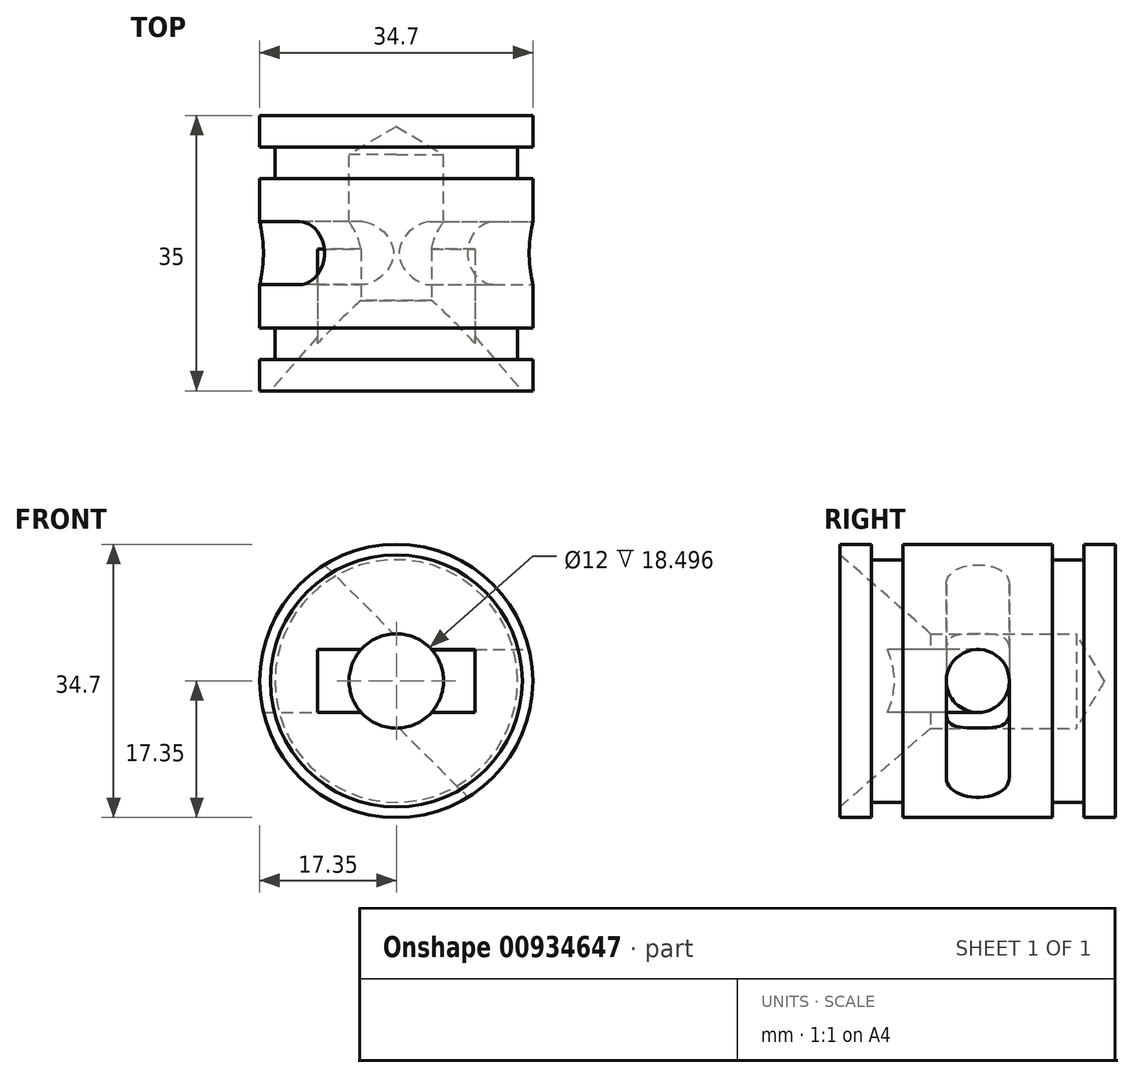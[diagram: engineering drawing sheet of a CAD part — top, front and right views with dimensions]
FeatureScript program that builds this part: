
annotation { "Feature Type Name" : "Feature", "Feature Type Description" : "" }
export const myFeature = defineFeature(function(context is Context, id is Id, definition is map)
    precondition{}
    {
        {
            var Q0;
            Q0=qCreatedBy(makeId("Front.planeOp"),FACE);
            var sketch = newSketch(context, id + "F0", { "sketchPlane" : qUnion([Q0])});
            skCircle(sketch, "E0", {"center": v(0, 0) * mm, "radius": 17.35 * mm});
            skCircle(sketch, "E1", {"center": v(0, 0) * mm, "radius": 16.35 * mm});
            skSolve(sketch);
        }
        {
            var Q0;
            Q0=makeQuery(id+"F0.imprint","IMPRINT",FACE,{"disambiguationData":[TD([[makeQuery(id+"F0.imprint","IMPRINT",EDGE,{"derivedFrom":sQuery(id+"F0.wireOp",EDGE,"E1")}),1.0]])]});
            var Q1;
            Q1=makeQuery(id+"F0.imprint","IMPRINT",FACE,{"disambiguationData":[TD([[makeQuery(id+"F0.imprint","IMPRINT",EDGE,{"derivedFrom":sQuery(id+"F0.wireOp",EDGE,"E0")}),1.0]])]});
            extrude(context, id + "F1", {"entities" : qUnion([Q0, Q1]), "oppositeDirection" : true, "depth" : 35 * mm, "offsetDistance" : 25 * mm, "symmetric" : true});
        }
        {
            var Q0;
            Q0=qCreatedBy(makeId("Right.planeOp"),FACE);
            var sketch = newSketch(context, id + "F2", { "sketchPlane" : qUnion([Q0])});
            skLineSegment(sketch, "E2.bottom", {"start": v(-13.5, 20.4) * mm, "end": v(-9.5, 20.4) * mm});
            skLineSegment(sketch, "E2.top", {"start": v(-13.5, 15.4) * mm, "end": v(-9.5, 15.4) * mm});
            skLineSegment(sketch, "E2.left", {"start": v(-13.5, 20.4) * mm, "end": v(-13.5, 15.4) * mm});
            skLineSegment(sketch, "E2.right", {"start": v(-9.5, 20.4) * mm, "end": v(-9.5, 15.4) * mm});
            skLineSegment(sketch, "E3.MirrorCS", {"start": v(13.5, 20.4) * mm, "end": v(9.5, 20.4) * mm});
            skLineSegment(sketch, "E4.MirrorCS", {"start": v(9.5, 20.4) * mm, "end": v(9.5, 15.4) * mm});
            skLineSegment(sketch, "E5.MirrorCS", {"start": v(13.5, 15.4) * mm, "end": v(9.5, 15.4) * mm});
            skLineSegment(sketch, "E6.MirrorCS", {"start": v(13.5, 20.4) * mm, "end": v(13.5, 15.4) * mm});
            skSolve(sketch);
        }
        {
            var Q0;
            Q0=makeQuery(id+"F2.imprint","IMPRINT",FACE,{"disambiguationData":[TD([[makeQuery(id+"F2.imprint","IMPRINT",EDGE,{"derivedFrom":sQuery(id+"F2.wireOp",EDGE,"E2.bottom")}),-1.0]])]});
            var Q1;
            Q1=makeQuery(id+"F2.imprint","IMPRINT",FACE,{"disambiguationData":[TD([[makeQuery(id+"F2.imprint","IMPRINT",EDGE,{"derivedFrom":sQuery(id+"F2.wireOp",EDGE,"E3.MirrorCS")}),1.0]])]});
            var Q2;
            Q2=makeQuery(id+"F1.opExtrude","SWEPT_FACE",FACE,{"disambiguationData":[OSD([sQuery(id+"F0.wireOp",EDGE,"E0")])]});
            revolve(context, id + "F3", {"operationType" : NewBodyOperationType.REMOVE, "surfaceOperationType" : NewSurfaceOperationType.NEW, "entities" : qUnion([Q0, Q1]), "axis" : qUnion([Q2]), "revolveType" : RevolveType.FULL, "oppositeDirection" : true});
        }
        {
            var Q0;
            Q0=makeQuery(id+"F1.opExtrude","CAP_FACE",FACE,{"disambiguationData":[OSD([sQuery(id+"F0.wireOp",EDGE,"E0")])],"isStart":true});
            var sketch = newSketch(context, id + "F4", { "sketchPlane" : qUnion([Q0])});
            skCircle(sketch, "E7", {"center": v(0, 0) * mm, "radius": 6 * mm});
            skLineSegment(sketch, "E8.bottom", {"start": v(10, -4) * mm, "end": v(-10, -4) * mm});
            skLineSegment(sketch, "E8.top", {"start": v(10, 4) * mm, "end": v(-10, 4) * mm});
            skLineSegment(sketch, "E8.left", {"start": v(10, -4) * mm, "end": v(10, 4) * mm});
            skLineSegment(sketch, "E8.right", {"start": v(-10, -4) * mm, "end": v(-10, 4) * mm});
            skSolve(sketch);
        }
        {
            var Q0;
            Q0=sQuery(id+"F4.wireOp",VERTEX,"E7.center");
            var Q1;
            Q1=makeQuery(id+"F1.opExtrude","SWEPT_BODY",BODY,{"disambiguationData":[OSD([sQuery(id+"F0.wireOp",EDGE,"E0")])]});
            hole(context, id + "F5", {"style" : HoleStyle.C_SINK, "endStyle" : HoleEndStyle.BLIND, "holeDiameter" : 12 * mm, "cSinkDiameter" : 32 * mm, "cSinkAngle" : 82 * degree, "majorDiameter" : 5 * mm, "holeDepth" : 30 * mm, "isTappedThrough" : true, "tappedDepth" : 40 * mm, "tapClearance" : 3, "startFromSketch" : true, "locations" : qUnion([Q0]), "scope" : qUnion([Q1])});
        }
        {
            var Q0;
            {var subQ5=sQuery(id+"F4.wireOp",EDGE,"E8.right");Q0=makeQuery(id+"F4.imprint","IMPRINT",FACE,{"disambiguationData":[TD([[makeQuery(id+"F4.imprint","IMPRINT",EDGE,{"derivedFrom":subQ5}),-1.0]])]});}
            var Q1;
            {var subQ5=sQuery(id+"F4.wireOp",EDGE,"E8.left");Q1=makeQuery(id+"F4.imprint","IMPRINT",FACE,{"disambiguationData":[TD([[makeQuery(id+"F4.imprint","IMPRINT",EDGE,{"derivedFrom":subQ5}),1.0]])]});}
            extrude(context, id + "F6", {"entities" : qUnion([Q0, Q1]), "operationType" : NewBodyOperationType.REMOVE, "oppositeDirection" : true, "depth" : 18 * mm, "offsetDistance" : 25 * mm});
        }
        {
            var Q0;
            Q0=qCreatedBy(makeId("Right.planeOp"),FACE);
            var sketch = newSketch(context, id + "F7", { "sketchPlane" : qUnion([Q0])});
            skCircle(sketch, "E9", {"center": v(0, 0) * mm, "radius": 4 * mm});
            skSolve(sketch);
        }
        {
            var Q0;
            Q0 = qSketchRegion(id + "F7", true);
            extrude(context, id + "F8", {"entities" : qUnion([Q0]), "operationType" : NewBodyOperationType.REMOVE, "oppositeDirection" : true, "depth" : 35 * mm, "offsetDistance" : 25 * mm, "symmetric" : true});
        }
        {
            var Q0;
            Q0=qCreatedBy(makeId("Right.planeOp"),FACE);
            var Q1;
            Q1=qCreatedBy(makeId("Top.planeOp"),FACE);
            cPlane(context, id + "F9", {"entities" : qUnion([Q0, Q1]), "cplaneType" : CPlaneType.MID_PLANE, "offset" : 25 * mm, "width" : 150 * mm, "height" : 150 * mm});
        }
        {
            var Q0;
            Q0=qCreatedBy(id+"F9.planeOp",FACE);
            var sketch = newSketch(context, id + "F10", { "sketchPlane" : qUnion([Q0])});
            skCircle(sketch, "E10", {"center": v(0, 0) * mm, "radius": 4 * mm});
            skSolve(sketch);
        }
        {
            var Q0;
            Q0=makeQuery(id+"F10.imprint","IMPRINT",FACE,{"disambiguationData":[TD([[makeQuery(id+"F10.imprint","IMPRINT",EDGE,{"derivedFrom":sQuery(id+"F10.wireOp",EDGE,"E10")}),1.0]])]});
            extrude(context, id + "F11", {"entities" : qUnion([Q0]), "operationType" : NewBodyOperationType.REMOVE, "oppositeDirection" : true, "depth" : 35 * mm, "offsetDistance" : 25 * mm, "symmetric" : true});
        }
        {
            var Q0;
            Q0=qCreatedBy(makeId("Front.planeOp"),FACE);
            var sketch = newSketch(context, id + "F12", { "sketchPlane" : qUnion([Q0])});
            skCircle(sketch, "E11.0", {"center": v(0, 0) * mm, "radius": 17.35 * mm});
            skLineSegment(sketch, "E12", {"start": v(-0.33, 6) * mm, "end": v(-9.1, 14.77) * mm});
            skLineSegment(sketch, "E13", {"start": v(-14.77, 9.1) * mm, "end": v(-9.66, 4) * mm});
            skLineSegment(sketch, "E14", {"start": v(14.77, -9.1) * mm, "end": v(9.66, -4) * mm});
            skLineSegment(sketch, "E15", {"start": v(0.33, -6) * mm, "end": v(9.1, -14.77) * mm});
            skLineSegment(sketch, "E16", {"start": v(0, 0) * mm, "end": v(-12.27, 12.27) * mm});
            skLineSegment(sketch, "E17", {"start": v(0, 0) * mm, "end": v(-17.35, 0) * mm});
            skLineSegment(sketch, "E18", {"start": v(0, 0) * mm, "end": v(12.27, -12.27) * mm});
            skLineSegment(sketch, "E19", {"start": v(0, 0) * mm, "end": v(17.35, 0) * mm});
            skSolve(sketch);
        }
        {
            var Q0;
            {var subQ2=sQuery(id+"F12.wireOp",EDGE,"E16");Q0=makeQuery(id+"F12.imprint","IMPRINT",FACE,{"disambiguationData":[TD([[makeQuery(id+"F12.imprint","IMPRINT",EDGE,{"derivedFrom":subQ2}),1.0]])]});}
            var Q1;
            {var subQ2=sQuery(id+"F12.wireOp",EDGE,"E18");Q1=makeQuery(id+"F12.imprint","IMPRINT",FACE,{"disambiguationData":[TD([[makeQuery(id+"F12.imprint","IMPRINT",EDGE,{"derivedFrom":subQ2}),1.0]])]});}
            extrude(context, id + "F13", {"entities" : qUnion([Q0, Q1]), "operationType" : NewBodyOperationType.REMOVE, "oppositeDirection" : true, "depth" : 8 * mm, "offsetDistance" : 25 * mm, "symmetric" : true});
        }
    });
